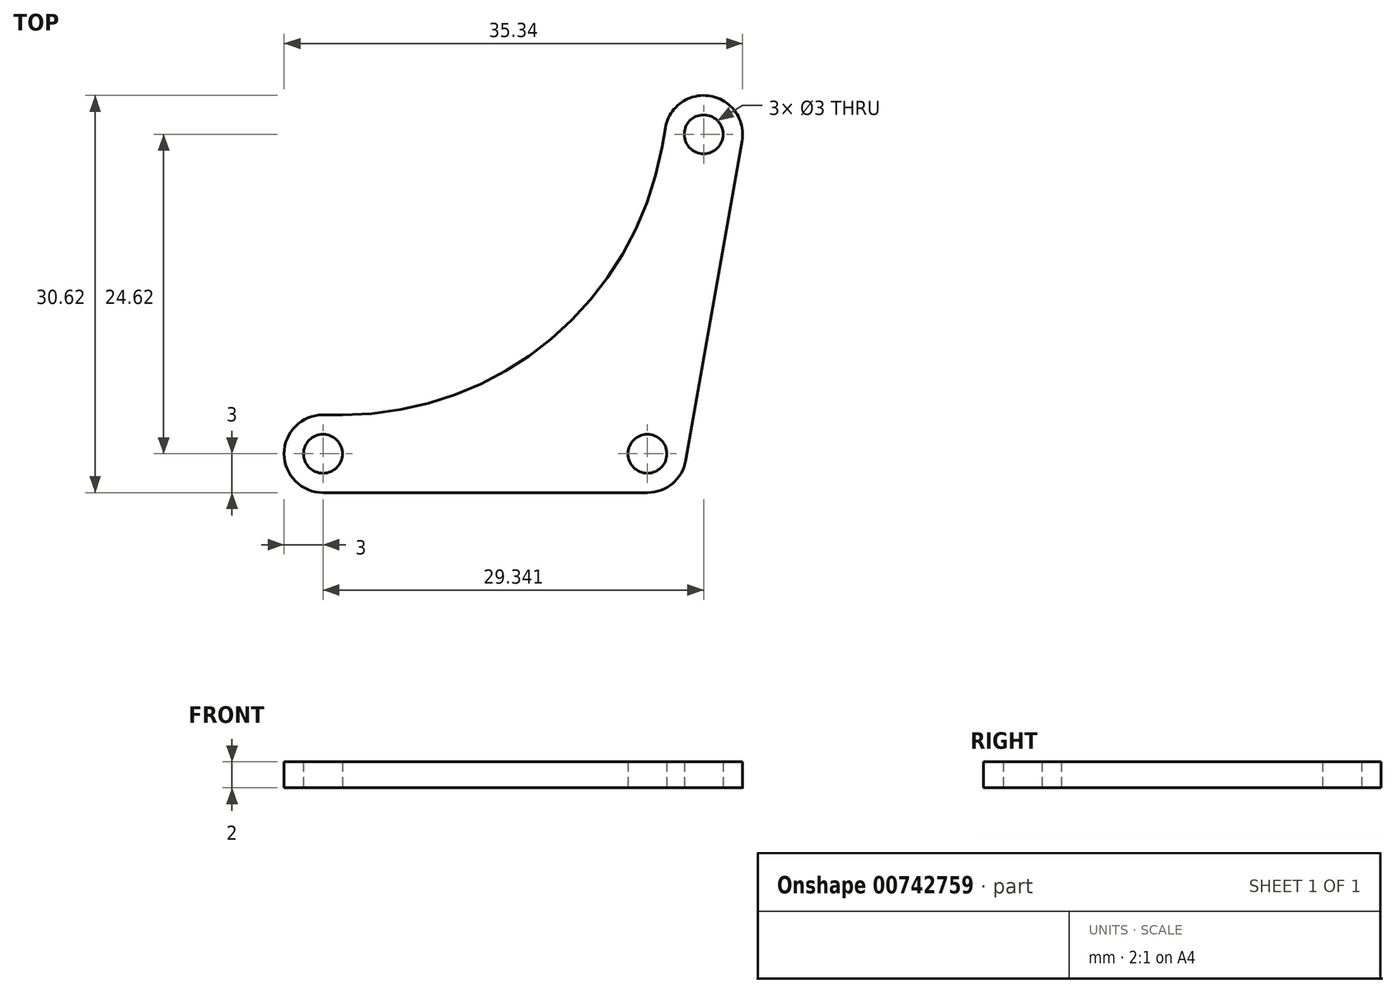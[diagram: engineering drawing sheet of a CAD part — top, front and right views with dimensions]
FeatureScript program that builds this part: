
annotation { "Feature Type Name" : "Feature", "Feature Type Description" : "" }
export const myFeature = defineFeature(function(context is Context, id is Id, definition is map)
    precondition{}
    {
        {
            var Q0;
            Q0=qCreatedBy(makeId("Top.planeOp"),FACE);
            var sketch = newSketch(context, id + "F0", { "sketchPlane" : qUnion([Q0])});
            skLineSegment(sketch, "E0", {"start": v(-25, 0) * mm, "end": v(0, 0) * mm, "construction": true});
            skLineSegment(sketch, "E1", {"start": v(0, 0) * mm, "end": v(4.34, 24.62) * mm, "construction": true});
            skArc(sketch, "E2.0.startCap", {"start": v(2.95, -0.52) * mm, "mid": v(1.93, -2.3) * mm, "end": v(0, -3) * mm});
            skArc(sketch, "E2.0.endCap", {"start": v(1.39, 25.14) * mm, "mid": v(4.86, 27.57) * mm, "end": v(7.3, 24.1) * mm});
            skLineSegment(sketch, "E2.0.left", {"start": v(1.13, 23.66) * mm, "end": v(1.39, 25.14) * mm});
            skLineSegment(sketch, "E2.0.right", {"start": v(2.95, -0.52) * mm, "end": v(7.3, 24.1) * mm});
            skArc(sketch, "E2.1.startCap", {"start": v(-25, -3) * mm, "mid": v(-28, 0) * mm, "end": v(-25, 3) * mm});
            skLineSegment(sketch, "E2.1.left", {"start": v(-25, 3) * mm, "end": v(-23.5, 3) * mm});
            skLineSegment(sketch, "E2.1.right", {"start": v(-25, -3) * mm, "end": v(0, -3) * mm});
            skCircle(sketch, "E3", {"center": v(-25, 0) * mm, "radius": 1.5 * mm});
            skCircle(sketch, "E4", {"center": v(4.34, 24.62) * mm, "radius": 1.5 * mm});
            skCircle(sketch, "E5", {"center": v(0, 0) * mm, "radius": 1.5 * mm});
            skPoint(sketch, "E6.visualSharp", {"position": v(-2.52, 3) * mm});
            skArc(sketch, "E6.filletArc", {"start": v(-23.5, 3) * mm, "mid": v(-7.43, 8.85) * mm, "end": v(1.13, 23.66) * mm});
            skSolve(sketch);
        }
        {
            var Q0;
            Q0 = qSketchRegion(id + "F0", true);
            extrude(context, id + "F1", {"entities" : qUnion([Q0]), "depth" : 2 * mm, "offsetDistance" : 25 * mm});
        }
    });
